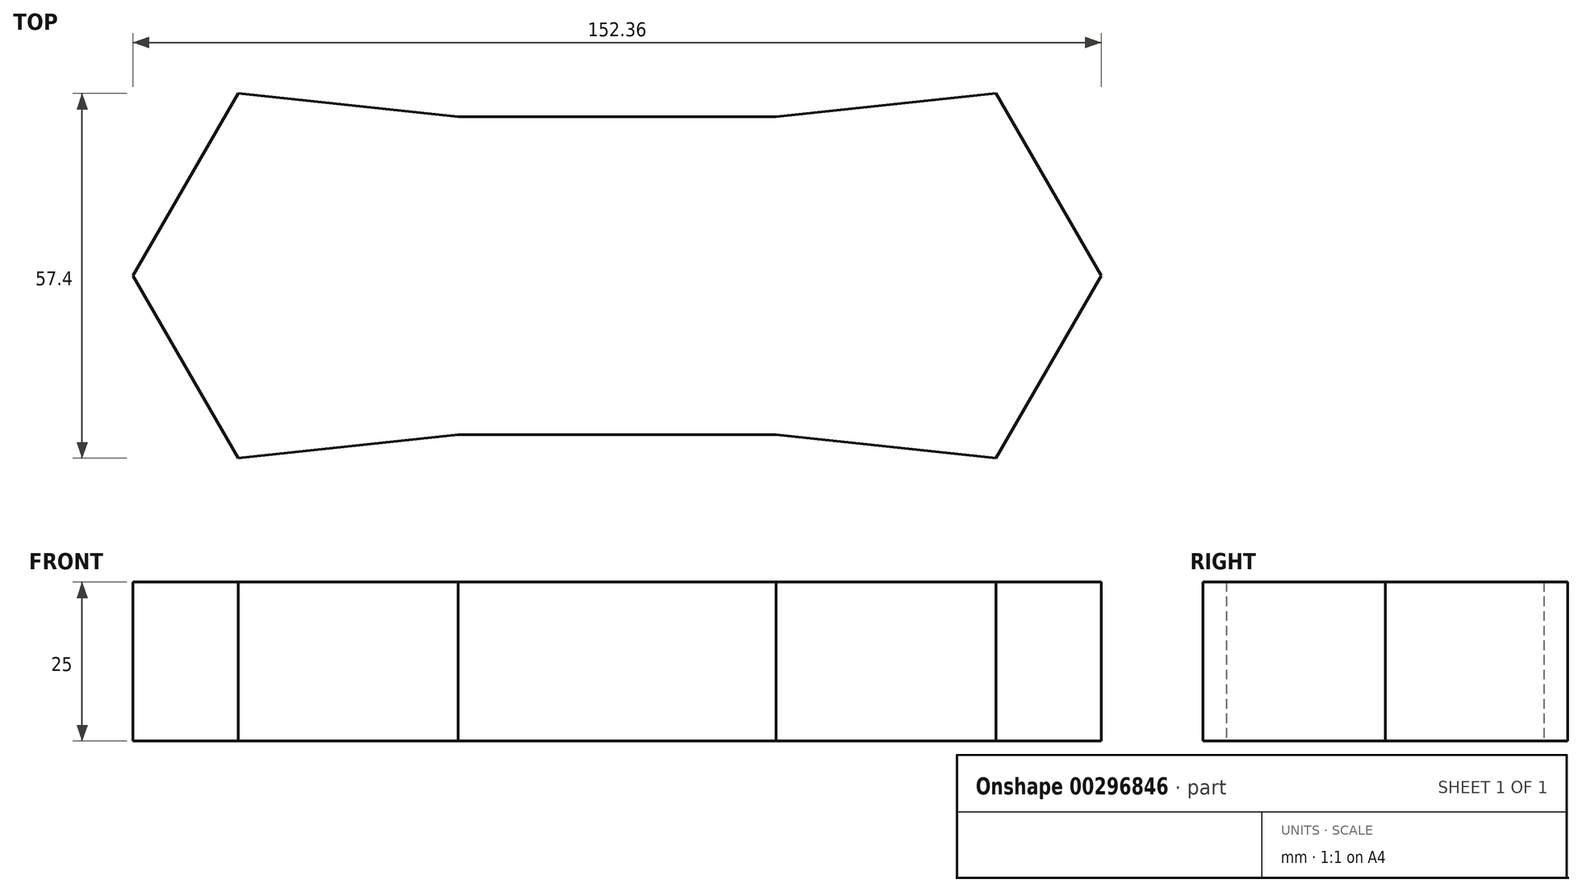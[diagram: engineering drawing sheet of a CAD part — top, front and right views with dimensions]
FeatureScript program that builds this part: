
annotation { "Feature Type Name" : "Feature", "Feature Type Description" : "" }
export const myFeature = defineFeature(function(context is Context, id is Id, definition is map)
    precondition{}
    {
        {
            var Q0;
            Q0=qCreatedBy(makeId("Top.planeOp"),FACE);
            var sketch = newSketch(context, id + "F0", { "sketchPlane" : qUnion([Q0])});
            skLineSegment(sketch, "E0.bottom", {"start": v(-25, -25) * mm, "end": v(25, -25) * mm});
            skLineSegment(sketch, "E0.top", {"start": v(-25, 25) * mm, "end": v(25, 25) * mm});
            skLineSegment(sketch, "E0.left", {"start": v(-25, -25) * mm, "end": v(-25, 25) * mm});
            skLineSegment(sketch, "E0.right", {"start": v(25, -25) * mm, "end": v(25, 25) * mm});
            skPoint(sketch, "E0.middle", {"position": v(0, 0) * mm});
            skCircle(sketch, "E1.cCircle", {"center": v(-43.04, 0) * mm, "radius": 33.14 * mm, "construction": true});
            skPoint(sketch, "E1.cCircle.centerSnap0", {"position": v(-43.04, 0) * mm});
            skLineSegment(sketch, "E1.0", {"start": v(-26.47, -28.7) * mm, "end": v(-59.61, -28.7) * mm});
            skLineSegment(sketch, "E1.1", {"start": v(-59.61, -28.7) * mm, "end": v(-76.18, 0) * mm});
            skLineSegment(sketch, "E1.2", {"start": v(-76.18, 0) * mm, "end": v(-59.61, 28.7) * mm});
            skLineSegment(sketch, "E1.3", {"start": v(-59.61, 28.7) * mm, "end": v(-26.47, 28.7) * mm});
            skLineSegment(sketch, "E1.4", {"start": v(-26.47, 28.7) * mm, "end": v(-9.9, 0) * mm});
            skLineSegment(sketch, "E1.5", {"start": v(-9.9, 0) * mm, "end": v(-26.47, -28.7) * mm});
            skLineSegment(sketch, "E2.MirrorCS", {"start": v(26.47, 28.7) * mm, "end": v(9.9, 0) * mm});
            skLineSegment(sketch, "E3.MirrorCS", {"start": v(9.9, 0) * mm, "end": v(26.47, -28.7) * mm});
            skLineSegment(sketch, "E4.MirrorCS", {"start": v(26.47, -28.7) * mm, "end": v(59.61, -28.7) * mm});
            skLineSegment(sketch, "E5.MirrorCS", {"start": v(59.61, -28.7) * mm, "end": v(76.18, 0) * mm});
            skLineSegment(sketch, "E6.MirrorCS", {"start": v(76.18, 0) * mm, "end": v(59.61, 28.7) * mm});
            skLineSegment(sketch, "E7.MirrorCS", {"start": v(59.61, 28.7) * mm, "end": v(26.47, 28.7) * mm});
            skLineSegment(sketch, "E8", {"start": v(-59.61, -28.7) * mm, "end": v(-25, -25) * mm});
            skLineSegment(sketch, "E9", {"start": v(-59.61, 28.7) * mm, "end": v(-25, 25) * mm});
            skLineSegment(sketch, "E10", {"start": v(59.61, -28.7) * mm, "end": v(25, -25) * mm});
            skLineSegment(sketch, "E11", {"start": v(59.61, 28.7) * mm, "end": v(25, 25) * mm});
            skSolve(sketch);
        }
        {
            var Q0;
            Q0=makeQuery(id+"F0.imprint","IMPRINT",FACE,{"disambiguationData":[TD([[makeQuery(id+"F0.imprint","IMPRINT",EDGE,{"derivedFrom":sQuery(id+"F0.wireOp",EDGE,"E0.left")}),1.0]])]});
            var Q1;
            {var subQ0=sQuery(id+"F0.wireOp",EDGE,"E1.5");var subQ5=sQuery(id+"F0.wireOp",EDGE,"E0.bottom");var subQ6=makeQuery(id+"F0.imprint","INTERSECT",VERTEX,{"derivedFrom":[subQ5,subQ0]});Q1=makeQuery(id+"F0.imprint","IMPRINT",FACE,{"disambiguationData":[TD([[makeQuery(id+"F0.imprint","IMPRINT",EDGE,{"disambiguationData":[TD([[subQ6,-1.0]])],"derivedFrom":subQ5}),1.0]])]});}
            var Q2;
            {var subQ0=sQuery(id+"F0.wireOp",EDGE,"E0.left");Q2=makeQuery(id+"F0.imprint","IMPRINT",FACE,{"disambiguationData":[TD([[makeQuery(id+"F0.imprint","IMPRINT",EDGE,{"derivedFrom":subQ0}),-1.0]])]});}
            var Q3;
            {var subQ0=sQuery(id+"F0.wireOp",EDGE,"E0.right");Q3=makeQuery(id+"F0.imprint","IMPRINT",FACE,{"disambiguationData":[TD([[makeQuery(id+"F0.imprint","IMPRINT",EDGE,{"derivedFrom":subQ0}),1.0]])]});}
            var Q4;
            Q4=makeQuery(id+"F0.imprint","IMPRINT",FACE,{"disambiguationData":[TD([[makeQuery(id+"F0.imprint","IMPRINT",EDGE,{"derivedFrom":sQuery(id+"F0.wireOp",EDGE,"E0.right")}),-1.0]])]});
            extrude(context, id + "F1", {"entities" : qUnion([Q0, Q1, Q2, Q3, Q4]), "depth" : 25 * mm});
        }
    });
